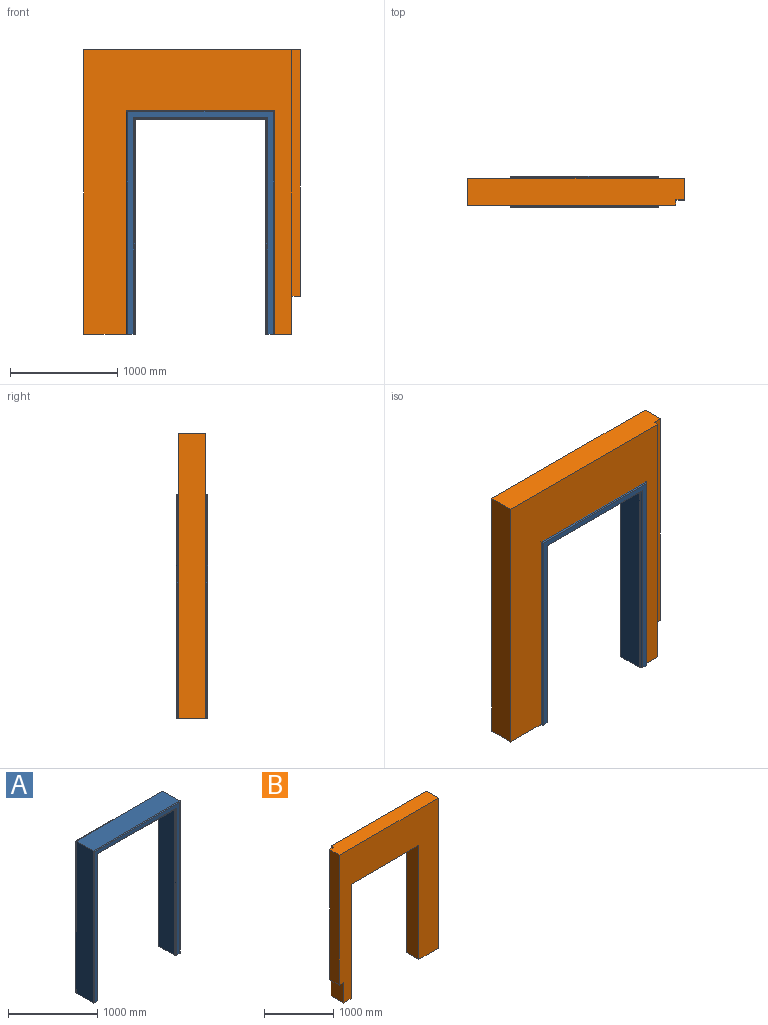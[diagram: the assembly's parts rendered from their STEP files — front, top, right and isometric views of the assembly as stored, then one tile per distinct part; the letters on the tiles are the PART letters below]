
ASSEMBLY  parts=2 mates=1
PART A: 30 faces, bbox 1380x290.1x2085 mm
  f0: cylinder r=10mm len=1380mm, axis (1,0,0), area 21519.9mm2, adj f9,f11,f14,f15
  f1: cylinder r=10mm len=1256mm, axis (-1,0,0), area 19572.1mm2, adj f2,f8,f15,f16
  f2: plane 1236x10mm, normal (0,0,-1), area 12360mm2, adj f1,f7,f17,f18
  f3: plane 1220x250mm, normal (0,0,-1), area 305000mm2, adj f6,f12,f18,f19
  f4: plane 1236x10mm, normal (0,0,-1), area 12360mm2, adj f5,f12,f20,f21
  f5: plane 2013x10mm, normal (-1,0,0), area 20130mm2, adj f4,f12,f22,f23
  f6: plane 2005x250mm, normal (-1,0,0), area 501250mm2, adj f3,f12,f18,f23
  f7: plane 2013x10mm, normal (-1,0,0), area 20130mm2, adj f2,f8,f18,f23
  f8: cylinder r=10mm len=2023mm, axis (0,0,1), area 31698.7mm2, adj f1,f7,f15,f23
  f9: cylinder r=10mm len=2085mm, axis (0,0,-1), area 32672.6mm2, adj f0,f10,f15,f23
  f10: plane 2085x270mm, normal (1,0,0), area 562950mm2, adj f9,f11,f23,f24
  f11: plane 1380x270mm, normal (0,0,1), area 372600mm2, adj f0,f10,f13,f25
  f12: plane 2013x1236mm, normal (0,-1,0), area 41968mm2, adj f3,f4,f5,f6,f19,f20,f23,f27
  f13: plane 2085x270mm, normal (-1,0,0), area 552547.7mm2, adj f11,f14,f26,f27
  f14: cylinder r=10mm len=2085mm, axis (0,0,1), area 32672.6mm2, adj f0,f13,f15,f27
  f15: plane 2075x1360mm, normal (0,1,0), area 281112mm2, adj f0,f1,f8,f9,f14,f16,f23,f27
  f16: cylinder r=10mm len=2023mm, axis (0,0,-1), area 31698.7mm2, adj f1,f15,f17,f27
  f17: plane 2013x10mm, normal (1,0,0), area 20130mm2, adj f2,f16,f18,f27
  f18: plane 2013x1236mm, normal (0,1,0), area 41968mm2, adj f2,f3,f6,f7,f17,f19,f23,f27
  f19: plane 2005x250mm, normal (1,0,0), area 501250mm2, adj f3,f12,f18,f27
  f20: plane 2013x10mm, normal (1,0,0), area 20130mm2, adj f4,f12,f27,f28
  f21: cylinder r=10mm len=1256mm, axis (1,0,0), area 19572.1mm2, adj f4,f22,f28,f29
  f22: cylinder r=10mm len=2023mm, axis (0,0,-1), area 31698.7mm2, adj f5,f21,f23,f29
  f23: plane 290.06x80.04mm, normal (0,0,-1), area 22794.2mm2, adj f5,f6,f7,f8,f9,f10,f12,f15
  f24: cylinder r=10mm len=2085mm, axis (0,0,1), area 32672.6mm2, adj f10,f23,f25,f29
  f25: cylinder r=10mm len=1380mm, axis (-1,0,0), area 21519.9mm2, adj f11,f24,f26,f29
  f26: cylinder r=10mm len=2085mm, axis (0,0,-1), area 32672.6mm2, adj f13,f25,f27,f29
  f27: plane 290x80mm, normal (0,0,-1), area 22793.9mm2, adj f12,f13,f14,f15,f16,f17,f18,f19
  f28: cylinder r=10mm len=2023mm, axis (0,0,1), area 31698.7mm2, adj f20,f21,f27,f29
  f29: plane 2075x1360mm, normal (0,-1,0), area 281112mm2, adj f21,f22,f23,f24,f25,f26,f27,f28
PART B: 13 faces, bbox 2022x250x2655 mm
  f0: plane 2300x80mm, normal (0,1,0), area 184000mm2, adj f5,f6,f7,f10
  f1: plane 1380x250mm, normal (0,0,-1), area 345000mm2, adj f2,f8,f9,f11
  f2: plane 2020x250mm, normal (-1,0,0), area 505000mm2, adj f1,f3,f9,f11
  f3: plane 400x250mm, normal (0,0,-1), area 100000mm2, adj f2,f4,f9,f11
  f4: plane 2655x250mm, normal (1,0,0), area 663750mm2, adj f3,f5,f9,f11
  f5: plane 2022x250mm, normal (0,0,1), area 501500mm2, adj f0,f4,f6,f9,f10,f11
  f6: plane 2300x200mm, normal (-1,0,0), area 460000mm2, adj f0,f5,f7,f11
  f7: plane 200x80mm, normal (0,0,-1), area 16000mm2, adj f0,f6,f10,f11
  f8: plane 2020x250mm, normal (1,0,0), area 505000mm2, adj f1,f9,f11,f12
  f9: plane 2655x1942mm, normal (0,1,0), area 2368410mm2, adj f1,f2,f3,f4,f5,f8,f10,f12
  f10: plane 2655x250mm, normal (-1,0,0), area 203750mm2, adj f0,f5,f7,f9,f11,f12
  f11: plane 2655x2022mm, normal (0,-1,0), area 2552410mm2, adj f1,f2,f3,f4,f5,f6,f7,f8
  f12: plane 250x162mm, normal (0,0,-1), area 40500mm2, adj f8,f9,f10,f11
PLACE A t=(-2644.59,1209.34,31.72)mm
PLACE B rot(axis=(0,0,1),180deg) t=(-1792.59,1084.34,31.72)mm
MATE fastened B.f8 <-> A.f10  axis (-1,0,0) through (-1954.59,1209.34,31.72)mm
